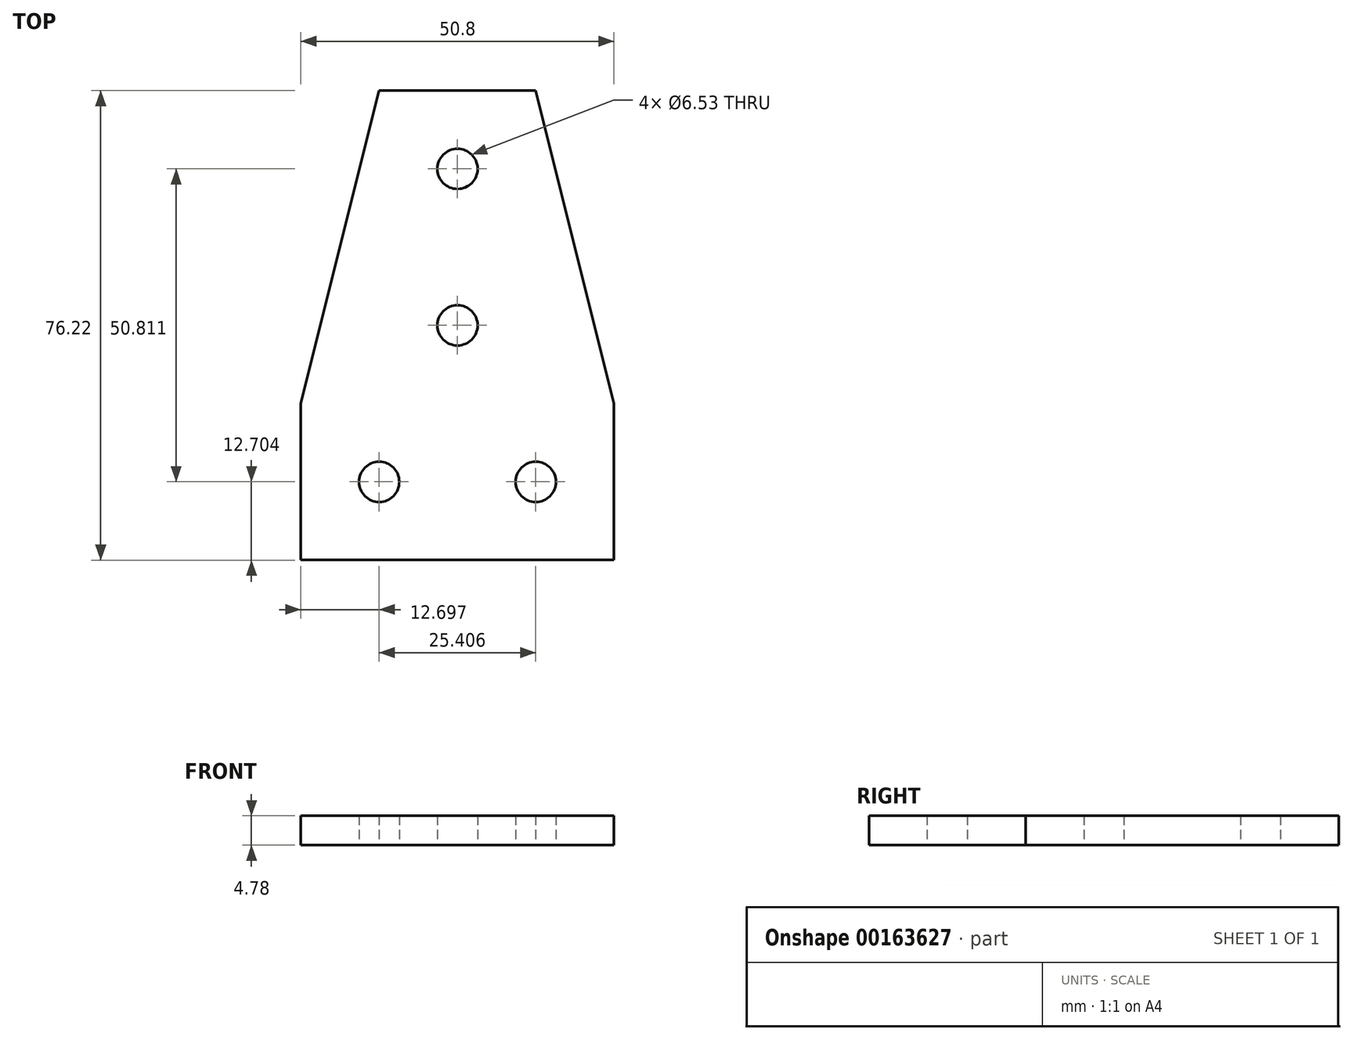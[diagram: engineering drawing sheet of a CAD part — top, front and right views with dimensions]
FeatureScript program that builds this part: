
annotation { "Feature Type Name" : "Feature", "Feature Type Description" : "" }
export const myFeature = defineFeature(function(context is Context, id is Id, definition is map)
    precondition{}
    {
        {
            var Q0;
            Q0=qCreatedBy(makeId("Top.planeOp"),FACE);
            var sketch = newSketch(context, id + "F0", { "sketchPlane" : qUnion([Q0])});
            skLineSegment(sketch, "E0.top", {"start": v(12.7, 38.1) * mm, "end": v(-12.7, 38.1) * mm});
            skPoint(sketch, "E0.middle", {"position": v(0, 0) * mm});
            skLineSegment(sketch, "E1", {"start": v(0, 0) * mm, "end": v(0, -44.44) * mm, "construction": true});
            skLineSegment(sketch, "E2", {"start": v(-25.4, -38.1) * mm, "end": v(-25.4, -12.7) * mm});
            skLineSegment(sketch, "E3", {"start": v(25.4, -12.7) * mm, "end": v(25.4, -38.1) * mm});
            skLineSegment(sketch, "E4", {"start": v(-25.4, -12.7) * mm, "end": v(-12.7, 38.1) * mm});
            skLineSegment(sketch, "E5", {"start": v(12.7, 38.1) * mm, "end": v(25.4, -12.7) * mm});
            skCircle(sketch, "E6", {"center": v(-12.7, -25.4) * mm, "radius": 3.26 * mm});
            skCircle(sketch, "E7.MirrorC", {"center": v(12.7, -25.4) * mm, "radius": 3.26 * mm});
            skLineSegment(sketch, "E8", {"start": v(-25.4, -38.1) * mm, "end": v(25.4, -38.1) * mm});
            skCircle(sketch, "E9", {"center": v(0, 0) * mm, "radius": 3.26 * mm});
            skCircle(sketch, "E10", {"center": v(0, 25.4) * mm, "radius": 3.26 * mm});
            skSolve(sketch);
        }
        {
            var Q0;
            Q0 = qSketchRegion(id + "F0", true);
            extrude(context, id + "F1", {"entities" : qUnion([Q0]), "depth" : 4.78 * mm});
        }
    });
